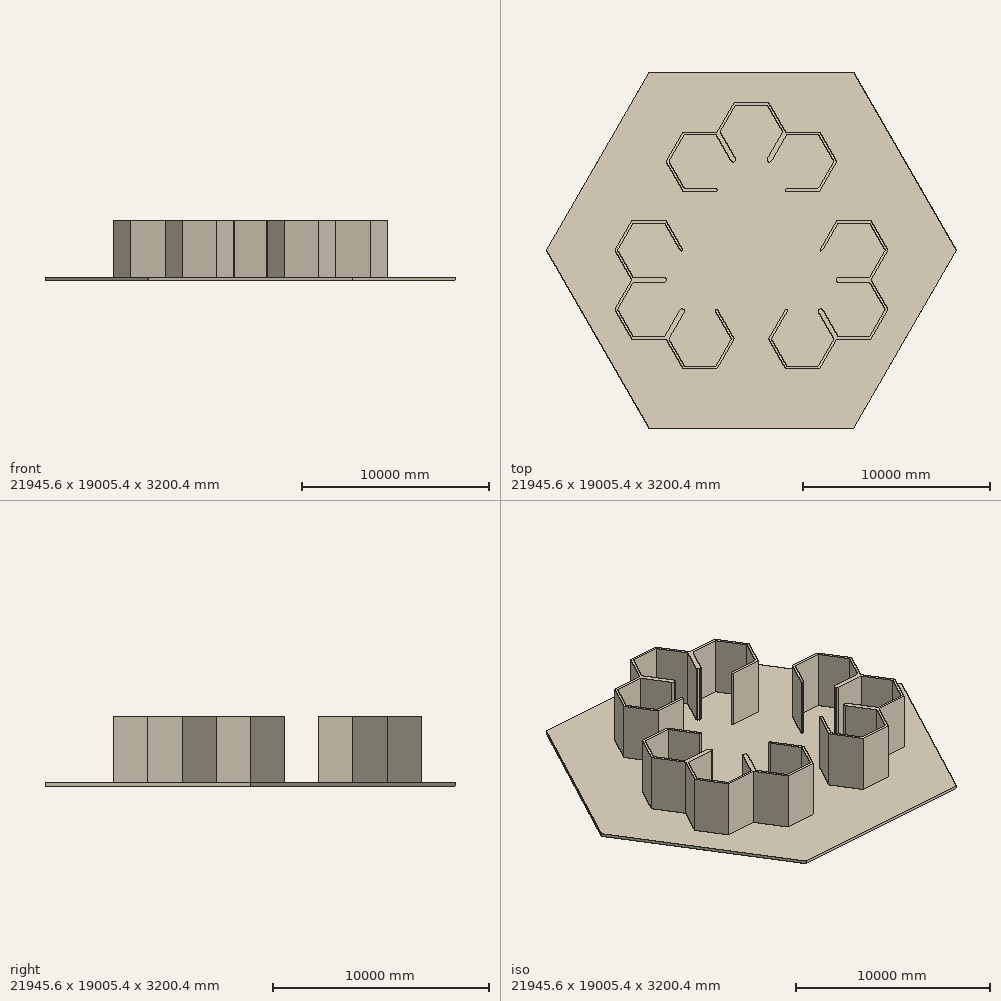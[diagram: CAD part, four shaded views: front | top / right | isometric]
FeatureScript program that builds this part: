
annotation { "Feature Type Name" : "Feature", "Feature Type Description" : "" }
export const myFeature = defineFeature(function(context is Context, id is Id, definition is map)
    precondition{}
    {
        {
            var Q0;
            Q0=qCreatedBy(makeId("Top.planeOp"),FACE);
            var sketch = newSketch(context, id + "F0", { "sketchPlane" : qUnion([Q0])});
            skLineSegment(sketch, "E0", {"start": v(0, 0) * mm, "end": v(1828.8, 0) * mm, "construction": true});
            skLineSegment(sketch, "E1", {"start": v(1828.8, 0) * mm, "end": v(3657.6, 0) * mm, "construction": true});
            skLineSegment(sketch, "E2", {"start": v(3657.6, 0) * mm, "end": v(5486.4, 0) * mm, "construction": true});
            skLineSegment(sketch, "E3", {"start": v(0, 0) * mm, "end": v(914.4, 1583.79) * mm, "construction": true});
            skLineSegment(sketch, "E4", {"start": v(914.4, 1583.79) * mm, "end": v(1828.8, 3167.57) * mm, "construction": true});
            skLineSegment(sketch, "E5", {"start": v(1828.8, 3167.57) * mm, "end": v(2743.2, 4751.36) * mm, "construction": true});
            skLineSegment(sketch, "E6", {"start": v(0, 0) * mm, "end": v(-914.4, 1583.79) * mm, "construction": true});
            skLineSegment(sketch, "E7", {"start": v(-914.4, 1583.79) * mm, "end": v(-1828.8, 3167.57) * mm, "construction": true});
            skLineSegment(sketch, "E8", {"start": v(-1828.8, 3167.57) * mm, "end": v(-2743.2, 4751.36) * mm, "construction": true});
            skLineSegment(sketch, "E9", {"start": v(0, 0) * mm, "end": v(-1828.8, 0) * mm, "construction": true});
            skLineSegment(sketch, "E10", {"start": v(-1828.8, 0) * mm, "end": v(-3657.6, 0) * mm, "construction": true});
            skLineSegment(sketch, "E11", {"start": v(-3657.6, 0) * mm, "end": v(-5486.4, 0) * mm, "construction": true});
            skLineSegment(sketch, "E12", {"start": v(0, 0) * mm, "end": v(-914.4, -1583.79) * mm, "construction": true});
            skLineSegment(sketch, "E13", {"start": v(-914.4, -1583.79) * mm, "end": v(-1828.8, -3167.57) * mm, "construction": true});
            skLineSegment(sketch, "E14", {"start": v(-1828.8, -3167.57) * mm, "end": v(-2743.2, -4751.36) * mm, "construction": true});
            skLineSegment(sketch, "E15", {"start": v(0, 0) * mm, "end": v(914.4, -1583.79) * mm, "construction": true});
            skLineSegment(sketch, "E16", {"start": v(914.4, -1583.79) * mm, "end": v(1828.8, -3167.57) * mm, "construction": true});
            skLineSegment(sketch, "E17", {"start": v(1828.8, -3167.57) * mm, "end": v(2743.2, -4751.36) * mm, "construction": true});
            skCircle(sketch, "E18.cCircle", {"center": v(0, 0) * mm, "radius": 1828.8 * mm, "construction": true});
            skLineSegment(sketch, "E18.0", {"start": v(1828.8, 0) * mm, "end": v(914.4, -1583.79) * mm});
            skLineSegment(sketch, "E18.1", {"start": v(914.4, -1583.79) * mm, "end": v(-914.4, -1583.79) * mm});
            skLineSegment(sketch, "E18.2", {"start": v(-914.4, -1583.79) * mm, "end": v(-1828.8, 0) * mm});
            skLineSegment(sketch, "E18.3", {"start": v(-1828.8, 0) * mm, "end": v(-914.4, 1583.79) * mm});
            skLineSegment(sketch, "E18.4", {"start": v(-914.4, 1583.79) * mm, "end": v(914.4, 1583.79) * mm});
            skLineSegment(sketch, "E18.5", {"start": v(914.4, 1583.79) * mm, "end": v(1828.8, 0) * mm});
            skLineSegment(sketch, "E19", {"start": v(914.4, -1583.79) * mm, "end": v(2743.2, -1583.79) * mm, "construction": true});
            skLineSegment(sketch, "E20", {"start": v(2743.2, -1583.79) * mm, "end": v(1828.8, 0) * mm, "construction": true});
            skCircle(sketch, "E21.cCircle", {"center": v(2743.2, -1583.79) * mm, "radius": 1828.8 * mm, "construction": true});
            skLineSegment(sketch, "E21.0", {"start": v(1828.8, 0) * mm, "end": v(3657.6, 0) * mm});
            skLineSegment(sketch, "E21.1", {"start": v(3657.6, 0) * mm, "end": v(4572, -1583.79) * mm});
            skLineSegment(sketch, "E21.2", {"start": v(4572, -1583.79) * mm, "end": v(3657.6, -3167.57) * mm});
            skLineSegment(sketch, "E21.3", {"start": v(3657.6, -3167.57) * mm, "end": v(1828.8, -3167.57) * mm});
            skLineSegment(sketch, "E21.4", {"start": v(1828.8, -3167.57) * mm, "end": v(914.4, -1583.79) * mm});
            skLineSegment(sketch, "E21.5", {"start": v(914.4, -1583.79) * mm, "end": v(1828.8, 0) * mm});
            skCircle(sketch, "E22.cCircle", {"center": v(5486.4, 0) * mm, "radius": 1828.8 * mm, "construction": true});
            skLineSegment(sketch, "E22.0", {"start": v(3657.6, 0) * mm, "end": v(4572, 1583.79) * mm});
            skLineSegment(sketch, "E22.1", {"start": v(4572, 1583.79) * mm, "end": v(6400.8, 1583.79) * mm});
            skLineSegment(sketch, "E22.2", {"start": v(6400.8, 1583.79) * mm, "end": v(7315.2, 0) * mm});
            skLineSegment(sketch, "E22.3", {"start": v(7315.2, 0) * mm, "end": v(6400.8, -1583.79) * mm});
            skLineSegment(sketch, "E22.4", {"start": v(6400.8, -1583.79) * mm, "end": v(4572, -1583.79) * mm});
            skLineSegment(sketch, "E22.5", {"start": v(4572, -1583.79) * mm, "end": v(3657.6, 0) * mm});
            skLineSegment(sketch, "E23", {"start": v(-914.4, -1583.79) * mm, "end": v(0, -3167.57) * mm, "construction": true});
            skLineSegment(sketch, "E24", {"start": v(914.4, -1583.79) * mm, "end": v(0, -3167.57) * mm, "construction": true});
            skCircle(sketch, "E25.cCircle", {"center": v(0, -3167.57) * mm, "radius": 1828.8 * mm, "construction": true});
            skLineSegment(sketch, "E25.0", {"start": v(914.4, -1583.79) * mm, "end": v(1828.8, -3167.57) * mm});
            skLineSegment(sketch, "E25.1", {"start": v(1828.8, -3167.57) * mm, "end": v(914.4, -4751.36) * mm});
            skLineSegment(sketch, "E25.2", {"start": v(914.4, -4751.36) * mm, "end": v(-914.4, -4751.36) * mm});
            skLineSegment(sketch, "E25.3", {"start": v(-914.4, -4751.36) * mm, "end": v(-1828.8, -3167.57) * mm});
            skLineSegment(sketch, "E25.4", {"start": v(-1828.8, -3167.57) * mm, "end": v(-914.4, -1583.79) * mm});
            skLineSegment(sketch, "E25.5", {"start": v(-914.4, -1583.79) * mm, "end": v(914.4, -1583.79) * mm});
            skLineSegment(sketch, "E26", {"start": v(1828.8, 0) * mm, "end": v(2743.2, 1583.79) * mm, "construction": true});
            skLineSegment(sketch, "E27", {"start": v(2743.2, 1583.79) * mm, "end": v(914.4, 1583.79) * mm, "construction": true});
            skLineSegment(sketch, "E28", {"start": v(914.4, 1583.79) * mm, "end": v(0, 3167.57) * mm, "construction": true});
            skLineSegment(sketch, "E29", {"start": v(0, 3167.57) * mm, "end": v(-914.4, 1583.79) * mm, "construction": true});
            skLineSegment(sketch, "E30", {"start": v(-914.4, 1583.79) * mm, "end": v(-2743.2, 1583.79) * mm, "construction": true});
            skLineSegment(sketch, "E31", {"start": v(-2743.2, 1583.79) * mm, "end": v(-1828.8, 0) * mm, "construction": true});
            skLineSegment(sketch, "E32", {"start": v(-1828.8, 0) * mm, "end": v(-2743.2, -1583.79) * mm, "construction": true});
            skLineSegment(sketch, "E33", {"start": v(-2743.2, -1583.79) * mm, "end": v(-914.4, -1583.79) * mm, "construction": true});
            skCircle(sketch, "E34.cCircle", {"center": v(2743.2, 1583.79) * mm, "radius": 1828.8 * mm, "construction": true});
            skLineSegment(sketch, "E34.0", {"start": v(914.4, 1583.79) * mm, "end": v(1828.8, 3167.57) * mm});
            skLineSegment(sketch, "E34.1", {"start": v(1828.8, 3167.57) * mm, "end": v(3657.6, 3167.57) * mm});
            skLineSegment(sketch, "E34.2", {"start": v(3657.6, 3167.57) * mm, "end": v(4572, 1583.79) * mm});
            skLineSegment(sketch, "E34.3", {"start": v(4572, 1583.79) * mm, "end": v(3657.6, 0) * mm});
            skLineSegment(sketch, "E34.4", {"start": v(3657.6, 0) * mm, "end": v(1828.8, 0) * mm});
            skLineSegment(sketch, "E34.5", {"start": v(1828.8, 0) * mm, "end": v(914.4, 1583.79) * mm});
            skCircle(sketch, "E35.cCircle", {"center": v(0, 3167.57) * mm, "radius": 1828.8 * mm, "construction": true});
            skLineSegment(sketch, "E35.0", {"start": v(-914.4, 1583.79) * mm, "end": v(-1828.8, 3167.57) * mm});
            skLineSegment(sketch, "E35.1", {"start": v(-1828.8, 3167.57) * mm, "end": v(-914.4, 4751.36) * mm});
            skLineSegment(sketch, "E35.2", {"start": v(-914.4, 4751.36) * mm, "end": v(914.4, 4751.36) * mm});
            skLineSegment(sketch, "E35.3", {"start": v(914.4, 4751.36) * mm, "end": v(1828.8, 3167.57) * mm});
            skLineSegment(sketch, "E35.4", {"start": v(1828.8, 3167.57) * mm, "end": v(914.4, 1583.79) * mm});
            skLineSegment(sketch, "E35.5", {"start": v(914.4, 1583.79) * mm, "end": v(-914.4, 1583.79) * mm});
            skCircle(sketch, "E36.cCircle", {"center": v(-2743.2, 1583.79) * mm, "radius": 1828.8 * mm, "construction": true});
            skLineSegment(sketch, "E36.0", {"start": v(-1828.8, 0) * mm, "end": v(-3657.6, 0) * mm});
            skLineSegment(sketch, "E36.1", {"start": v(-3657.6, 0) * mm, "end": v(-4572, 1583.79) * mm});
            skLineSegment(sketch, "E36.2", {"start": v(-4572, 1583.79) * mm, "end": v(-3657.6, 3167.57) * mm});
            skLineSegment(sketch, "E36.3", {"start": v(-3657.6, 3167.57) * mm, "end": v(-1828.8, 3167.57) * mm});
            skLineSegment(sketch, "E36.4", {"start": v(-1828.8, 3167.57) * mm, "end": v(-914.4, 1583.79) * mm});
            skLineSegment(sketch, "E36.5", {"start": v(-914.4, 1583.79) * mm, "end": v(-1828.8, 0) * mm});
            skCircle(sketch, "E37.cCircle", {"center": v(-2743.2, -1583.79) * mm, "radius": 1828.8 * mm, "construction": true});
            skLineSegment(sketch, "E37.0", {"start": v(-914.4, -1583.79) * mm, "end": v(-1828.8, -3167.57) * mm});
            skLineSegment(sketch, "E37.1", {"start": v(-1828.8, -3167.57) * mm, "end": v(-3657.6, -3167.57) * mm});
            skLineSegment(sketch, "E37.2", {"start": v(-3657.6, -3167.57) * mm, "end": v(-4572, -1583.79) * mm});
            skLineSegment(sketch, "E37.3", {"start": v(-4572, -1583.79) * mm, "end": v(-3657.6, 0) * mm});
            skLineSegment(sketch, "E37.4", {"start": v(-3657.6, 0) * mm, "end": v(-1828.8, 0) * mm});
            skLineSegment(sketch, "E37.5", {"start": v(-1828.8, 0) * mm, "end": v(-914.4, -1583.79) * mm});
            skCircle(sketch, "E38.cCircle", {"center": v(-2743.2, 4751.36) * mm, "radius": 1828.8 * mm, "construction": true});
            skLineSegment(sketch, "E38.0", {"start": v(-1828.8, 3167.57) * mm, "end": v(-3657.6, 3167.57) * mm});
            skLineSegment(sketch, "E38.1", {"start": v(-3657.6, 3167.57) * mm, "end": v(-4572, 4751.36) * mm});
            skLineSegment(sketch, "E38.2", {"start": v(-4572, 4751.36) * mm, "end": v(-3657.6, 6335.15) * mm});
            skLineSegment(sketch, "E38.3", {"start": v(-3657.6, 6335.15) * mm, "end": v(-1828.8, 6335.15) * mm});
            skLineSegment(sketch, "E38.4", {"start": v(-1828.8, 6335.15) * mm, "end": v(-914.4, 4751.36) * mm});
            skLineSegment(sketch, "E38.5", {"start": v(-914.4, 4751.36) * mm, "end": v(-1828.8, 3167.57) * mm});
            skCircle(sketch, "E39.cCircle", {"center": v(2743.2, 4751.36) * mm, "radius": 1828.8 * mm, "construction": true});
            skLineSegment(sketch, "E39.0", {"start": v(1828.8, 3167.57) * mm, "end": v(914.4, 4751.36) * mm});
            skLineSegment(sketch, "E39.1", {"start": v(914.4, 4751.36) * mm, "end": v(1828.8, 6335.15) * mm});
            skLineSegment(sketch, "E39.2", {"start": v(1828.8, 6335.15) * mm, "end": v(3657.6, 6335.15) * mm});
            skLineSegment(sketch, "E39.3", {"start": v(3657.6, 6335.15) * mm, "end": v(4572, 4751.36) * mm});
            skLineSegment(sketch, "E39.4", {"start": v(4572, 4751.36) * mm, "end": v(3657.6, 3167.57) * mm});
            skLineSegment(sketch, "E39.5", {"start": v(3657.6, 3167.57) * mm, "end": v(1828.8, 3167.57) * mm});
            skCircle(sketch, "E40.cCircle", {"center": v(-2743.2, -4751.36) * mm, "radius": 1828.8 * mm, "construction": true});
            skLineSegment(sketch, "E40.0", {"start": v(-1828.8, -3167.57) * mm, "end": v(-914.4, -4751.36) * mm});
            skLineSegment(sketch, "E40.1", {"start": v(-914.4, -4751.36) * mm, "end": v(-1828.8, -6335.15) * mm});
            skLineSegment(sketch, "E40.2", {"start": v(-1828.8, -6335.15) * mm, "end": v(-3657.6, -6335.15) * mm});
            skLineSegment(sketch, "E40.3", {"start": v(-3657.6, -6335.15) * mm, "end": v(-4572, -4751.36) * mm});
            skLineSegment(sketch, "E40.4", {"start": v(-4572, -4751.36) * mm, "end": v(-3657.6, -3167.57) * mm});
            skLineSegment(sketch, "E40.5", {"start": v(-3657.6, -3167.57) * mm, "end": v(-1828.8, -3167.57) * mm});
            skCircle(sketch, "E41.cCircle", {"center": v(-5486.4, 0) * mm, "radius": 1828.8 * mm, "construction": true});
            skLineSegment(sketch, "E41.0", {"start": v(-3657.6, 0) * mm, "end": v(-4572, -1583.79) * mm});
            skLineSegment(sketch, "E41.1", {"start": v(-4572, -1583.79) * mm, "end": v(-6400.8, -1583.79) * mm});
            skLineSegment(sketch, "E41.2", {"start": v(-6400.8, -1583.79) * mm, "end": v(-7315.2, 0) * mm});
            skLineSegment(sketch, "E41.3", {"start": v(-7315.2, 0) * mm, "end": v(-6400.8, 1583.79) * mm});
            skLineSegment(sketch, "E41.4", {"start": v(-6400.8, 1583.79) * mm, "end": v(-4572, 1583.79) * mm});
            skLineSegment(sketch, "E41.5", {"start": v(-4572, 1583.79) * mm, "end": v(-3657.6, 0) * mm});
            skLineSegment(sketch, "E42", {"start": v(-3657.6, -3167.57) * mm, "end": v(-5486.4, -3167.57) * mm, "construction": true});
            skLineSegment(sketch, "E43", {"start": v(-5486.4, -3167.57) * mm, "end": v(-4572, -1583.79) * mm, "construction": true});
            skCircle(sketch, "E44.cCircle", {"center": v(-5486.4, -3167.57) * mm, "radius": 1828.8 * mm, "construction": true});
            skLineSegment(sketch, "E44.0", {"start": v(-4572, -1583.79) * mm, "end": v(-3657.6, -3167.57) * mm});
            skLineSegment(sketch, "E44.1", {"start": v(-3657.6, -3167.57) * mm, "end": v(-4572, -4751.36) * mm});
            skLineSegment(sketch, "E44.2", {"start": v(-4572, -4751.36) * mm, "end": v(-6400.8, -4751.36) * mm});
            skLineSegment(sketch, "E44.3", {"start": v(-6400.8, -4751.36) * mm, "end": v(-7315.2, -3167.57) * mm});
            skLineSegment(sketch, "E44.4", {"start": v(-7315.2, -3167.57) * mm, "end": v(-6400.8, -1583.79) * mm});
            skLineSegment(sketch, "E44.5", {"start": v(-6400.8, -1583.79) * mm, "end": v(-4572, -1583.79) * mm});
            skLineSegment(sketch, "E45", {"start": v(-4572, 1583.79) * mm, "end": v(-5486.4, 3167.57) * mm, "construction": true});
            skPoint(sketch, "E45.endSnap0", {"position": v(-5486.4, 1583.79) * mm});
            skLineSegment(sketch, "E46", {"start": v(-5486.4, 3167.57) * mm, "end": v(-3657.6, 3167.57) * mm, "construction": true});
            skCircle(sketch, "E47.cCircle", {"center": v(-5486.4, 3167.57) * mm, "radius": 1828.8 * mm, "construction": true});
            skLineSegment(sketch, "E47.0", {"start": v(-3657.6, 3167.57) * mm, "end": v(-4572, 1583.79) * mm});
            skLineSegment(sketch, "E47.1", {"start": v(-4572, 1583.79) * mm, "end": v(-6400.8, 1583.79) * mm});
            skLineSegment(sketch, "E47.2", {"start": v(-6400.8, 1583.79) * mm, "end": v(-7315.2, 3167.57) * mm});
            skLineSegment(sketch, "E47.3", {"start": v(-7315.2, 3167.57) * mm, "end": v(-6400.8, 4751.36) * mm});
            skLineSegment(sketch, "E47.4", {"start": v(-6400.8, 4751.36) * mm, "end": v(-4572, 4751.36) * mm});
            skLineSegment(sketch, "E47.5", {"start": v(-4572, 4751.36) * mm, "end": v(-3657.6, 3167.57) * mm});
            skLineSegment(sketch, "E48", {"start": v(-914.4, 4751.36) * mm, "end": v(0, 6335.15) * mm, "construction": true});
            skLineSegment(sketch, "E49", {"start": v(0, 6335.15) * mm, "end": v(914.4, 4751.36) * mm, "construction": true});
            skLineSegment(sketch, "E50", {"start": v(3657.6, 3167.57) * mm, "end": v(5486.4, 3167.57) * mm, "construction": true});
            skLineSegment(sketch, "E51", {"start": v(5486.4, 3167.57) * mm, "end": v(4572, 1583.79) * mm, "construction": true});
            skLineSegment(sketch, "E52", {"start": v(4572, -1583.79) * mm, "end": v(5486.4, -3167.57) * mm, "construction": true});
            skLineSegment(sketch, "E53", {"start": v(5486.4, -3167.57) * mm, "end": v(3657.6, -3167.57) * mm, "construction": true});
            skLineSegment(sketch, "E54", {"start": v(-914.4, -4751.36) * mm, "end": v(0, -6335.15) * mm, "construction": true});
            skLineSegment(sketch, "E55", {"start": v(0, -6335.15) * mm, "end": v(914.4, -4751.36) * mm, "construction": true});
            skCircle(sketch, "E56.cCircle", {"center": v(2743.2, -4751.36) * mm, "radius": 1828.8 * mm, "construction": true});
            skLineSegment(sketch, "E56.0", {"start": v(1828.8, -3167.57) * mm, "end": v(3657.6, -3167.57) * mm});
            skLineSegment(sketch, "E56.1", {"start": v(3657.6, -3167.57) * mm, "end": v(4572, -4751.36) * mm});
            skLineSegment(sketch, "E56.2", {"start": v(4572, -4751.36) * mm, "end": v(3657.6, -6335.15) * mm});
            skLineSegment(sketch, "E56.3", {"start": v(3657.6, -6335.15) * mm, "end": v(1828.8, -6335.15) * mm});
            skLineSegment(sketch, "E56.4", {"start": v(1828.8, -6335.15) * mm, "end": v(914.4, -4751.36) * mm});
            skLineSegment(sketch, "E56.5", {"start": v(914.4, -4751.36) * mm, "end": v(1828.8, -3167.57) * mm});
            skCircle(sketch, "E57.cCircle", {"center": v(0, -6335.15) * mm, "radius": 1828.8 * mm, "construction": true});
            skLineSegment(sketch, "E57.0", {"start": v(914.4, -4751.36) * mm, "end": v(1828.8, -6335.15) * mm});
            skLineSegment(sketch, "E57.1", {"start": v(1828.8, -6335.15) * mm, "end": v(914.4, -7918.94) * mm});
            skLineSegment(sketch, "E57.2", {"start": v(914.4, -7918.94) * mm, "end": v(-914.4, -7918.94) * mm});
            skLineSegment(sketch, "E57.3", {"start": v(-914.4, -7918.94) * mm, "end": v(-1828.8, -6335.15) * mm});
            skLineSegment(sketch, "E57.4", {"start": v(-1828.8, -6335.15) * mm, "end": v(-914.4, -4751.36) * mm});
            skLineSegment(sketch, "E57.5", {"start": v(-914.4, -4751.36) * mm, "end": v(914.4, -4751.36) * mm});
            skCircle(sketch, "E58.cCircle", {"center": v(5486.4, -3167.57) * mm, "radius": 1828.8 * mm, "construction": true});
            skLineSegment(sketch, "E58.0", {"start": v(4572, -1583.79) * mm, "end": v(6400.8, -1583.79) * mm});
            skLineSegment(sketch, "E58.1", {"start": v(6400.8, -1583.79) * mm, "end": v(7315.2, -3167.57) * mm});
            skLineSegment(sketch, "E58.2", {"start": v(7315.2, -3167.57) * mm, "end": v(6400.8, -4751.36) * mm});
            skLineSegment(sketch, "E58.3", {"start": v(6400.8, -4751.36) * mm, "end": v(4572, -4751.36) * mm});
            skLineSegment(sketch, "E58.4", {"start": v(4572, -4751.36) * mm, "end": v(3657.6, -3167.57) * mm});
            skLineSegment(sketch, "E58.5", {"start": v(3657.6, -3167.57) * mm, "end": v(4572, -1583.79) * mm});
            skCircle(sketch, "E59.cCircle", {"center": v(5486.4, 3167.57) * mm, "radius": 1828.8 * mm, "construction": true});
            skLineSegment(sketch, "E59.0", {"start": v(3657.6, 3167.57) * mm, "end": v(4572, 4751.36) * mm});
            skLineSegment(sketch, "E59.1", {"start": v(4572, 4751.36) * mm, "end": v(6400.8, 4751.36) * mm});
            skLineSegment(sketch, "E59.2", {"start": v(6400.8, 4751.36) * mm, "end": v(7315.2, 3167.57) * mm});
            skLineSegment(sketch, "E59.3", {"start": v(7315.2, 3167.57) * mm, "end": v(6400.8, 1583.79) * mm});
            skLineSegment(sketch, "E59.4", {"start": v(6400.8, 1583.79) * mm, "end": v(4572, 1583.79) * mm});
            skLineSegment(sketch, "E59.5", {"start": v(4572, 1583.79) * mm, "end": v(3657.6, 3167.57) * mm});
            skCircle(sketch, "E60.cCircle", {"center": v(0, 6335.15) * mm, "radius": 1828.8 * mm, "construction": true});
            skLineSegment(sketch, "E60.0", {"start": v(-914.4, 4751.36) * mm, "end": v(-1828.8, 6335.15) * mm});
            skLineSegment(sketch, "E60.1", {"start": v(-1828.8, 6335.15) * mm, "end": v(-914.4, 7918.94) * mm});
            skLineSegment(sketch, "E60.2", {"start": v(-914.4, 7918.94) * mm, "end": v(914.4, 7918.94) * mm});
            skLineSegment(sketch, "E60.3", {"start": v(914.4, 7918.94) * mm, "end": v(1828.8, 6335.15) * mm});
            skLineSegment(sketch, "E60.4", {"start": v(1828.8, 6335.15) * mm, "end": v(914.4, 4751.36) * mm});
            skLineSegment(sketch, "E60.5", {"start": v(914.4, 4751.36) * mm, "end": v(-914.4, 4751.36) * mm});
            skLineSegment(sketch, "E61", {"start": v(-4572, 4751.36) * mm, "end": v(-5486.4, 6335.15) * mm, "construction": true});
            skPoint(sketch, "E61.endSnap0", {"position": v(-5486.4, 4751.36) * mm});
            skLineSegment(sketch, "E62", {"start": v(-5486.4, 6335.15) * mm, "end": v(-3657.6, 6335.15) * mm, "construction": true});
            skLineSegment(sketch, "E63", {"start": v(-1828.8, 6335.15) * mm, "end": v(-2743.2, 7918.94) * mm, "construction": true});
            skPoint(sketch, "E63.endSnap0", {"position": v(-2743.2, 6335.15) * mm});
            skLineSegment(sketch, "E64", {"start": v(-2743.2, 7918.94) * mm, "end": v(-3657.6, 6335.15) * mm, "construction": true});
            skLineSegment(sketch, "E65", {"start": v(-7315.2, 0) * mm, "end": v(-8229.6, 1583.79) * mm, "construction": true});
            skLineSegment(sketch, "E66", {"start": v(-8229.6, 1583.79) * mm, "end": v(-6400.8, 1583.79) * mm, "construction": true});
            skLineSegment(sketch, "E67", {"start": v(-8229.6, -1583.79) * mm, "end": v(-6400.8, -1583.79) * mm, "construction": true});
            skLineSegment(sketch, "E68", {"start": v(-7315.2, 0) * mm, "end": v(-8229.6, -1583.79) * mm, "construction": true});
            skLineSegment(sketch, "E69", {"start": v(-4572, -4751.36) * mm, "end": v(-5486.4, -6335.15) * mm, "construction": true});
            skPoint(sketch, "E69.endSnap0", {"position": v(-5486.4, -4751.36) * mm});
            skLineSegment(sketch, "E70", {"start": v(-5486.4, -6335.15) * mm, "end": v(-3657.6, -6335.15) * mm, "construction": true});
            skLineSegment(sketch, "E71", {"start": v(-1828.8, -6335.15) * mm, "end": v(-2743.2, -7918.94) * mm, "construction": true});
            skPoint(sketch, "E71.endSnap0", {"position": v(-2743.2, -6335.15) * mm});
            skLineSegment(sketch, "E72", {"start": v(-2743.2, -7918.94) * mm, "end": v(-3657.6, -6335.15) * mm, "construction": true});
            skLineSegment(sketch, "E73", {"start": v(1828.8, 6335.15) * mm, "end": v(2743.2, 7918.94) * mm, "construction": true});
            skLineSegment(sketch, "E74", {"start": v(2743.2, 7918.94) * mm, "end": v(3657.6, 6335.15) * mm, "construction": true});
            skLineSegment(sketch, "E75", {"start": v(3657.6, 6335.15) * mm, "end": v(5486.4, 6335.15) * mm, "construction": true});
            skPoint(sketch, "E75.endSnap0", {"position": v(5486.4, 4751.36) * mm});
            skLineSegment(sketch, "E76", {"start": v(5486.4, 6335.15) * mm, "end": v(4572, 4751.36) * mm, "construction": true});
            skLineSegment(sketch, "E77", {"start": v(7315.2, 0) * mm, "end": v(8229.6, 1583.79) * mm, "construction": true});
            skLineSegment(sketch, "E78", {"start": v(8229.6, 1583.79) * mm, "end": v(6400.8, 1583.79) * mm, "construction": true});
            skLineSegment(sketch, "E79", {"start": v(6400.8, -1583.79) * mm, "end": v(8229.6, -1583.79) * mm, "construction": true});
            skLineSegment(sketch, "E80", {"start": v(8229.6, -1583.79) * mm, "end": v(7315.2, 0) * mm, "construction": true});
            skLineSegment(sketch, "E81", {"start": v(1828.8, -6335.15) * mm, "end": v(2743.2, -7918.94) * mm, "construction": true});
            skPoint(sketch, "E81.endSnap0", {"position": v(2743.2, -6335.15) * mm});
            skLineSegment(sketch, "E82", {"start": v(2743.2, -7918.94) * mm, "end": v(3657.6, -6335.15) * mm, "construction": true});
            skLineSegment(sketch, "E83", {"start": v(4572, -4751.36) * mm, "end": v(5486.4, -6335.15) * mm, "construction": true});
            skPoint(sketch, "E83.endSnap0", {"position": v(5486.4, -4751.36) * mm});
            skLineSegment(sketch, "E84", {"start": v(5486.4, -6335.15) * mm, "end": v(3657.6, -6335.15) * mm, "construction": true});
            skCircle(sketch, "E85.cCircle", {"center": v(-2743.2, 7918.94) * mm, "radius": 1828.8 * mm, "construction": true});
            skLineSegment(sketch, "E85.0", {"start": v(-1828.8, 6335.15) * mm, "end": v(-3657.6, 6335.15) * mm});
            skLineSegment(sketch, "E85.1", {"start": v(-3657.6, 6335.15) * mm, "end": v(-4572, 7918.94) * mm});
            skLineSegment(sketch, "E85.2", {"start": v(-4572, 7918.94) * mm, "end": v(-3657.6, 9502.72) * mm});
            skLineSegment(sketch, "E85.3", {"start": v(-3657.6, 9502.72) * mm, "end": v(-1828.8, 9502.72) * mm});
            skLineSegment(sketch, "E85.4", {"start": v(-1828.8, 9502.72) * mm, "end": v(-914.4, 7918.94) * mm});
            skLineSegment(sketch, "E85.5", {"start": v(-914.4, 7918.94) * mm, "end": v(-1828.8, 6335.15) * mm});
            skCircle(sketch, "E86.cCircle", {"center": v(-5486.4, 6335.15) * mm, "radius": 1828.8 * mm, "construction": true});
            skLineSegment(sketch, "E86.0", {"start": v(-4572, 4751.36) * mm, "end": v(-6400.8, 4751.36) * mm});
            skLineSegment(sketch, "E86.1", {"start": v(-6400.8, 4751.36) * mm, "end": v(-7315.2, 6335.15) * mm});
            skLineSegment(sketch, "E86.2", {"start": v(-7315.2, 6335.15) * mm, "end": v(-6400.8, 7918.94) * mm});
            skLineSegment(sketch, "E86.3", {"start": v(-6400.8, 7918.94) * mm, "end": v(-4572, 7918.94) * mm});
            skLineSegment(sketch, "E86.4", {"start": v(-4572, 7918.94) * mm, "end": v(-3657.6, 6335.15) * mm});
            skLineSegment(sketch, "E86.5", {"start": v(-3657.6, 6335.15) * mm, "end": v(-4572, 4751.36) * mm});
            skCircle(sketch, "E87.cCircle", {"center": v(2743.2, 7918.94) * mm, "radius": 1828.8 * mm, "construction": true});
            skLineSegment(sketch, "E87.0", {"start": v(1828.8, 6335.15) * mm, "end": v(914.4, 7918.94) * mm});
            skLineSegment(sketch, "E87.1", {"start": v(914.4, 7918.94) * mm, "end": v(1828.8, 9502.72) * mm});
            skLineSegment(sketch, "E87.2", {"start": v(1828.8, 9502.72) * mm, "end": v(3657.6, 9502.72) * mm});
            skLineSegment(sketch, "E87.3", {"start": v(3657.6, 9502.72) * mm, "end": v(4572, 7918.94) * mm});
            skLineSegment(sketch, "E87.4", {"start": v(4572, 7918.94) * mm, "end": v(3657.6, 6335.15) * mm});
            skLineSegment(sketch, "E87.5", {"start": v(3657.6, 6335.15) * mm, "end": v(1828.8, 6335.15) * mm});
            skCircle(sketch, "E88.cCircle", {"center": v(5486.4, 6335.15) * mm, "radius": 1828.8 * mm, "construction": true});
            skLineSegment(sketch, "E88.0", {"start": v(4572, 4751.36) * mm, "end": v(3657.6, 6335.15) * mm});
            skLineSegment(sketch, "E88.1", {"start": v(3657.6, 6335.15) * mm, "end": v(4572, 7918.94) * mm});
            skLineSegment(sketch, "E88.2", {"start": v(4572, 7918.94) * mm, "end": v(6400.8, 7918.94) * mm});
            skLineSegment(sketch, "E88.3", {"start": v(6400.8, 7918.94) * mm, "end": v(7315.2, 6335.15) * mm});
            skLineSegment(sketch, "E88.4", {"start": v(7315.2, 6335.15) * mm, "end": v(6400.8, 4751.36) * mm});
            skLineSegment(sketch, "E88.5", {"start": v(6400.8, 4751.36) * mm, "end": v(4572, 4751.36) * mm});
            skCircle(sketch, "E89.cCircle", {"center": v(8229.6, -1583.79) * mm, "radius": 1828.8 * mm, "construction": true});
            skLineSegment(sketch, "E89.0", {"start": v(6400.8, -1583.79) * mm, "end": v(7315.2, 0) * mm});
            skLineSegment(sketch, "E89.1", {"start": v(7315.2, 0) * mm, "end": v(9144, 0) * mm});
            skLineSegment(sketch, "E89.2", {"start": v(9144, 0) * mm, "end": v(10058.4, -1583.79) * mm});
            skLineSegment(sketch, "E89.3", {"start": v(10058.4, -1583.79) * mm, "end": v(9144, -3167.57) * mm});
            skLineSegment(sketch, "E89.4", {"start": v(9144, -3167.57) * mm, "end": v(7315.2, -3167.57) * mm});
            skLineSegment(sketch, "E89.5", {"start": v(7315.2, -3167.57) * mm, "end": v(6400.8, -1583.79) * mm});
            skCircle(sketch, "E90.cCircle", {"center": v(8229.6, 1583.79) * mm, "radius": 1828.8 * mm, "construction": true});
            skLineSegment(sketch, "E90.0", {"start": v(6400.8, 1583.79) * mm, "end": v(7315.2, 3167.57) * mm});
            skLineSegment(sketch, "E90.1", {"start": v(7315.2, 3167.57) * mm, "end": v(9144, 3167.57) * mm});
            skLineSegment(sketch, "E90.2", {"start": v(9144, 3167.57) * mm, "end": v(10058.4, 1583.79) * mm});
            skLineSegment(sketch, "E90.3", {"start": v(10058.4, 1583.79) * mm, "end": v(9144, 0) * mm});
            skLineSegment(sketch, "E90.4", {"start": v(9144, 0) * mm, "end": v(7315.2, 0) * mm});
            skLineSegment(sketch, "E90.5", {"start": v(7315.2, 0) * mm, "end": v(6400.8, 1583.79) * mm});
            skCircle(sketch, "E91.cCircle", {"center": v(5486.4, -6335.15) * mm, "radius": 1828.8 * mm, "construction": true});
            skLineSegment(sketch, "E91.0", {"start": v(4572, -4751.36) * mm, "end": v(6400.8, -4751.36) * mm});
            skLineSegment(sketch, "E91.1", {"start": v(6400.8, -4751.36) * mm, "end": v(7315.2, -6335.15) * mm});
            skLineSegment(sketch, "E91.2", {"start": v(7315.2, -6335.15) * mm, "end": v(6400.8, -7918.94) * mm});
            skLineSegment(sketch, "E91.3", {"start": v(6400.8, -7918.94) * mm, "end": v(4572, -7918.94) * mm});
            skLineSegment(sketch, "E91.4", {"start": v(4572, -7918.94) * mm, "end": v(3657.6, -6335.15) * mm});
            skLineSegment(sketch, "E91.5", {"start": v(3657.6, -6335.15) * mm, "end": v(4572, -4751.36) * mm});
            skCircle(sketch, "E92.cCircle", {"center": v(2743.2, -7918.94) * mm, "radius": 1828.8 * mm, "construction": true});
            skLineSegment(sketch, "E92.0", {"start": v(1828.8, -6335.15) * mm, "end": v(3657.6, -6335.15) * mm});
            skLineSegment(sketch, "E92.1", {"start": v(3657.6, -6335.15) * mm, "end": v(4572, -7918.94) * mm});
            skLineSegment(sketch, "E92.2", {"start": v(4572, -7918.94) * mm, "end": v(3657.6, -9502.72) * mm});
            skLineSegment(sketch, "E92.3", {"start": v(3657.6, -9502.72) * mm, "end": v(1828.8, -9502.72) * mm});
            skLineSegment(sketch, "E92.4", {"start": v(1828.8, -9502.72) * mm, "end": v(914.4, -7918.94) * mm});
            skLineSegment(sketch, "E92.5", {"start": v(914.4, -7918.94) * mm, "end": v(1828.8, -6335.15) * mm});
            skCircle(sketch, "E93.cCircle", {"center": v(-2743.2, -7918.94) * mm, "radius": 1828.8 * mm, "construction": true});
            skLineSegment(sketch, "E93.0", {"start": v(-1828.8, -6335.15) * mm, "end": v(-914.4, -7918.94) * mm});
            skLineSegment(sketch, "E93.1", {"start": v(-914.4, -7918.94) * mm, "end": v(-1828.8, -9502.72) * mm});
            skLineSegment(sketch, "E93.2", {"start": v(-1828.8, -9502.72) * mm, "end": v(-3657.6, -9502.72) * mm});
            skLineSegment(sketch, "E93.3", {"start": v(-3657.6, -9502.72) * mm, "end": v(-4572, -7918.94) * mm});
            skLineSegment(sketch, "E93.4", {"start": v(-4572, -7918.94) * mm, "end": v(-3657.6, -6335.15) * mm});
            skLineSegment(sketch, "E93.5", {"start": v(-3657.6, -6335.15) * mm, "end": v(-1828.8, -6335.15) * mm});
            skCircle(sketch, "E94.cCircle", {"center": v(-5486.4, -6335.15) * mm, "radius": 1828.8 * mm, "construction": true});
            skLineSegment(sketch, "E94.0", {"start": v(-4572, -4751.36) * mm, "end": v(-3657.6, -6335.15) * mm});
            skLineSegment(sketch, "E94.1", {"start": v(-3657.6, -6335.15) * mm, "end": v(-4572, -7918.94) * mm});
            skLineSegment(sketch, "E94.2", {"start": v(-4572, -7918.94) * mm, "end": v(-6400.8, -7918.94) * mm});
            skLineSegment(sketch, "E94.3", {"start": v(-6400.8, -7918.94) * mm, "end": v(-7315.2, -6335.15) * mm});
            skLineSegment(sketch, "E94.4", {"start": v(-7315.2, -6335.15) * mm, "end": v(-6400.8, -4751.36) * mm});
            skLineSegment(sketch, "E94.5", {"start": v(-6400.8, -4751.36) * mm, "end": v(-4572, -4751.36) * mm});
            skCircle(sketch, "E95.cCircle", {"center": v(-8229.6, -1583.79) * mm, "radius": 1828.8 * mm, "construction": true});
            skLineSegment(sketch, "E95.0", {"start": v(-7315.2, 0) * mm, "end": v(-6400.8, -1583.79) * mm});
            skLineSegment(sketch, "E95.1", {"start": v(-6400.8, -1583.79) * mm, "end": v(-7315.2, -3167.57) * mm});
            skLineSegment(sketch, "E95.2", {"start": v(-7315.2, -3167.57) * mm, "end": v(-9144, -3167.57) * mm});
            skLineSegment(sketch, "E95.3", {"start": v(-9144, -3167.57) * mm, "end": v(-10058.4, -1583.79) * mm});
            skLineSegment(sketch, "E95.4", {"start": v(-10058.4, -1583.79) * mm, "end": v(-9144, 0) * mm});
            skLineSegment(sketch, "E95.5", {"start": v(-9144, 0) * mm, "end": v(-7315.2, 0) * mm});
            skCircle(sketch, "E96.cCircle", {"center": v(-8229.6, 1583.79) * mm, "radius": 1828.8 * mm, "construction": true});
            skLineSegment(sketch, "E96.0", {"start": v(-6400.8, 1583.79) * mm, "end": v(-7315.2, 0) * mm});
            skLineSegment(sketch, "E96.1", {"start": v(-7315.2, 0) * mm, "end": v(-9144, 0) * mm});
            skLineSegment(sketch, "E96.2", {"start": v(-9144, 0) * mm, "end": v(-10058.4, 1583.79) * mm});
            skLineSegment(sketch, "E96.3", {"start": v(-10058.4, 1583.79) * mm, "end": v(-9144, 3167.57) * mm});
            skLineSegment(sketch, "E96.4", {"start": v(-9144, 3167.57) * mm, "end": v(-7315.2, 3167.57) * mm});
            skLineSegment(sketch, "E96.5", {"start": v(-7315.2, 3167.57) * mm, "end": v(-6400.8, 1583.79) * mm});
            skLineSegment(sketch, "E97", {"start": v(-9144, 0) * mm, "end": v(-10972.8, 0) * mm, "construction": true});
            skCircle(sketch, "E98.cCircle", {"center": v(0, 0) * mm, "radius": 10972.8 * mm, "construction": true});
            skLineSegment(sketch, "E98.0", {"start": v(-10972.8, 0) * mm, "end": v(-5486.4, 9502.72) * mm});
            skLineSegment(sketch, "E98.1", {"start": v(-5486.4, 9502.72) * mm, "end": v(5486.4, 9502.72) * mm});
            skLineSegment(sketch, "E98.2", {"start": v(5486.4, 9502.72) * mm, "end": v(10972.8, 0) * mm});
            skLineSegment(sketch, "E98.3", {"start": v(10972.8, 0) * mm, "end": v(5486.4, -9502.72) * mm});
            skLineSegment(sketch, "E98.4", {"start": v(5486.4, -9502.72) * mm, "end": v(-5486.4, -9502.72) * mm});
            skLineSegment(sketch, "E98.5", {"start": v(-5486.4, -9502.72) * mm, "end": v(-10972.8, 0) * mm});
            skCircle(sketch, "E99.cCircle", {"center": v(-2743.2, 4751.36) * mm, "radius": 1676.4 * mm, "construction": true});
            skLineSegment(sketch, "E99.0", {"start": v(-1905, 3299.56) * mm, "end": v(-3581.4, 3299.56) * mm});
            skLineSegment(sketch, "E99.1", {"start": v(-3581.4, 3299.56) * mm, "end": v(-4419.6, 4751.36) * mm});
            skLineSegment(sketch, "E99.2", {"start": v(-4419.6, 4751.36) * mm, "end": v(-3581.4, 6203.17) * mm});
            skLineSegment(sketch, "E99.3", {"start": v(-3581.4, 6203.17) * mm, "end": v(-1905, 6203.17) * mm});
            skLineSegment(sketch, "E99.4", {"start": v(-1905, 6203.17) * mm, "end": v(-1066.8, 4751.36) * mm});
            skLineSegment(sketch, "E99.5", {"start": v(-1066.8, 4751.36) * mm, "end": v(-1905, 3299.56) * mm});
            skCircle(sketch, "E100.cCircle", {"center": v(0, 6335.15) * mm, "radius": 1676.4 * mm, "construction": true});
            skLineSegment(sketch, "E100.0", {"start": v(-838.2, 4883.34) * mm, "end": v(-1676.4, 6335.15) * mm});
            skLineSegment(sketch, "E100.1", {"start": v(-1676.4, 6335.15) * mm, "end": v(-838.2, 7786.95) * mm});
            skLineSegment(sketch, "E100.2", {"start": v(-838.2, 7786.95) * mm, "end": v(838.2, 7786.95) * mm});
            skLineSegment(sketch, "E100.3", {"start": v(838.2, 7786.95) * mm, "end": v(1676.4, 6335.15) * mm});
            skLineSegment(sketch, "E100.4", {"start": v(1676.4, 6335.15) * mm, "end": v(838.2, 4883.34) * mm});
            skLineSegment(sketch, "E100.5", {"start": v(838.2, 4883.34) * mm, "end": v(-838.2, 4883.34) * mm});
            skCircle(sketch, "E101.cCircle", {"center": v(2743.2, 4751.36) * mm, "radius": 1676.4 * mm, "construction": true});
            skLineSegment(sketch, "E101.0", {"start": v(1905, 3299.56) * mm, "end": v(1066.8, 4751.36) * mm});
            skLineSegment(sketch, "E101.1", {"start": v(1066.8, 4751.36) * mm, "end": v(1905, 6203.17) * mm});
            skLineSegment(sketch, "E101.2", {"start": v(1905, 6203.17) * mm, "end": v(3581.4, 6203.17) * mm});
            skLineSegment(sketch, "E101.3", {"start": v(3581.4, 6203.17) * mm, "end": v(4419.6, 4751.36) * mm});
            skLineSegment(sketch, "E101.4", {"start": v(4419.6, 4751.36) * mm, "end": v(3581.4, 3299.56) * mm});
            skLineSegment(sketch, "E101.5", {"start": v(3581.4, 3299.56) * mm, "end": v(1905, 3299.56) * mm});
            skCircle(sketch, "E102.cCircle", {"center": v(5486.4, 0) * mm, "radius": 1676.4 * mm, "construction": true});
            skLineSegment(sketch, "E102.0", {"start": v(3810, 0) * mm, "end": v(4648.2, 1451.8) * mm});
            skLineSegment(sketch, "E102.1", {"start": v(4648.2, 1451.8) * mm, "end": v(6324.6, 1451.8) * mm});
            skLineSegment(sketch, "E102.2", {"start": v(6324.6, 1451.8) * mm, "end": v(7162.8, 0) * mm});
            skLineSegment(sketch, "E102.3", {"start": v(7162.8, 0) * mm, "end": v(6324.6, -1451.8) * mm});
            skLineSegment(sketch, "E102.4", {"start": v(6324.6, -1451.8) * mm, "end": v(4648.2, -1451.8) * mm});
            skLineSegment(sketch, "E102.5", {"start": v(4648.2, -1451.8) * mm, "end": v(3810, 0) * mm});
            skCircle(sketch, "E103.cCircle", {"center": v(5486.4, -3167.57) * mm, "radius": 1676.4 * mm, "construction": true});
            skLineSegment(sketch, "E103.0", {"start": v(4648.2, -1715.77) * mm, "end": v(6324.6, -1715.77) * mm});
            skLineSegment(sketch, "E103.1", {"start": v(6324.6, -1715.77) * mm, "end": v(7162.8, -3167.57) * mm});
            skLineSegment(sketch, "E103.2", {"start": v(7162.8, -3167.57) * mm, "end": v(6324.6, -4619.38) * mm});
            skLineSegment(sketch, "E103.3", {"start": v(6324.6, -4619.38) * mm, "end": v(4648.2, -4619.38) * mm});
            skLineSegment(sketch, "E103.4", {"start": v(4648.2, -4619.38) * mm, "end": v(3810, -3167.57) * mm});
            skLineSegment(sketch, "E103.5", {"start": v(3810, -3167.57) * mm, "end": v(4648.2, -1715.77) * mm});
            skCircle(sketch, "E104.cCircle", {"center": v(2743.2, -4751.36) * mm, "radius": 1676.4 * mm, "construction": true});
            skLineSegment(sketch, "E104.0", {"start": v(1905, -3299.56) * mm, "end": v(3581.4, -3299.56) * mm});
            skLineSegment(sketch, "E104.1", {"start": v(3581.4, -3299.56) * mm, "end": v(4419.6, -4751.36) * mm});
            skLineSegment(sketch, "E104.2", {"start": v(4419.6, -4751.36) * mm, "end": v(3581.4, -6203.17) * mm});
            skLineSegment(sketch, "E104.3", {"start": v(3581.4, -6203.17) * mm, "end": v(1905, -6203.17) * mm});
            skLineSegment(sketch, "E104.4", {"start": v(1905, -6203.17) * mm, "end": v(1066.8, -4751.36) * mm});
            skLineSegment(sketch, "E104.5", {"start": v(1066.8, -4751.36) * mm, "end": v(1905, -3299.56) * mm});
            skCircle(sketch, "E105.cCircle", {"center": v(-2743.2, -4751.36) * mm, "radius": 1676.4 * mm, "construction": true});
            skLineSegment(sketch, "E105.0", {"start": v(-1905, -3299.56) * mm, "end": v(-1066.8, -4751.36) * mm});
            skLineSegment(sketch, "E105.1", {"start": v(-1066.8, -4751.36) * mm, "end": v(-1905, -6203.17) * mm});
            skLineSegment(sketch, "E105.2", {"start": v(-1905, -6203.17) * mm, "end": v(-3581.4, -6203.17) * mm});
            skLineSegment(sketch, "E105.3", {"start": v(-3581.4, -6203.17) * mm, "end": v(-4419.6, -4751.36) * mm});
            skLineSegment(sketch, "E105.4", {"start": v(-4419.6, -4751.36) * mm, "end": v(-3581.4, -3299.56) * mm});
            skLineSegment(sketch, "E105.5", {"start": v(-3581.4, -3299.56) * mm, "end": v(-1905, -3299.56) * mm});
            skCircle(sketch, "E106.cCircle", {"center": v(-5486.4, -3167.57) * mm, "radius": 1676.4 * mm, "construction": true});
            skLineSegment(sketch, "E106.0", {"start": v(-4648.2, -1715.77) * mm, "end": v(-3810, -3167.57) * mm});
            skLineSegment(sketch, "E106.1", {"start": v(-3810, -3167.57) * mm, "end": v(-4648.2, -4619.38) * mm});
            skLineSegment(sketch, "E106.2", {"start": v(-4648.2, -4619.38) * mm, "end": v(-6324.6, -4619.38) * mm});
            skLineSegment(sketch, "E106.3", {"start": v(-6324.6, -4619.38) * mm, "end": v(-7162.8, -3167.57) * mm});
            skLineSegment(sketch, "E106.4", {"start": v(-7162.8, -3167.57) * mm, "end": v(-6324.6, -1715.77) * mm});
            skLineSegment(sketch, "E106.5", {"start": v(-6324.6, -1715.77) * mm, "end": v(-4648.2, -1715.77) * mm});
            skCircle(sketch, "E107.cCircle", {"center": v(-5486.4, 0) * mm, "radius": 1676.4 * mm, "construction": true});
            skLineSegment(sketch, "E107.0", {"start": v(-3810, 0) * mm, "end": v(-4648.2, -1451.8) * mm});
            skLineSegment(sketch, "E107.1", {"start": v(-4648.2, -1451.8) * mm, "end": v(-6324.6, -1451.8) * mm});
            skLineSegment(sketch, "E107.2", {"start": v(-6324.6, -1451.8) * mm, "end": v(-7162.8, 0) * mm});
            skLineSegment(sketch, "E107.3", {"start": v(-7162.8, 0) * mm, "end": v(-6324.6, 1451.8) * mm});
            skLineSegment(sketch, "E107.4", {"start": v(-6324.6, 1451.8) * mm, "end": v(-4648.2, 1451.8) * mm});
            skLineSegment(sketch, "E107.5", {"start": v(-4648.2, 1451.8) * mm, "end": v(-3810, 0) * mm});
            skLineSegment(sketch, "E108", {"start": v(-1066.8, 4751.36) * mm, "end": v(-952.5, 4685.37) * mm});
            skLineSegment(sketch, "E109", {"start": v(-1905, 3299.56) * mm, "end": v(-1790.7, 3233.57) * mm});
            skLineSegment(sketch, "E110", {"start": v(-838.2, 4883.34) * mm, "end": v(-838.2, 4751.36) * mm});
            skLineSegment(sketch, "E111", {"start": v(838.2, 4883.34) * mm, "end": v(838.2, 4751.36) * mm});
            skLineSegment(sketch, "E112", {"start": v(1066.8, 4751.36) * mm, "end": v(952.5, 4685.37) * mm});
            skLineSegment(sketch, "E113", {"start": v(1905, 3299.56) * mm, "end": v(1790.7, 3233.57) * mm});
            skLineSegment(sketch, "E114", {"start": v(3810, 0) * mm, "end": v(3695.7, -66) * mm});
            skLineSegment(sketch, "E115", {"start": v(4648.2, -1451.8) * mm, "end": v(4533.9, -1517.8) * mm});
            skLineSegment(sketch, "E116", {"start": v(4648.2, -1715.77) * mm, "end": v(4533.9, -1649.78) * mm});
            skLineSegment(sketch, "E117", {"start": v(3810, -3167.57) * mm, "end": v(3695.7, -3101.58) * mm});
            skLineSegment(sketch, "E118", {"start": v(3581.4, -3299.56) * mm, "end": v(3581.4, -3167.57) * mm});
            skLineSegment(sketch, "E119", {"start": v(1905, -3299.56) * mm, "end": v(1905, -3167.57) * mm});
            skLineSegment(sketch, "E120", {"start": v(-3810, 0) * mm, "end": v(-3695.7, -66) * mm});
            skLineSegment(sketch, "E121", {"start": v(-4648.2, -1451.8) * mm, "end": v(-4533.9, -1517.8) * mm});
            skLineSegment(sketch, "E122", {"start": v(-4648.2, -1715.77) * mm, "end": v(-4533.9, -1649.78) * mm});
            skLineSegment(sketch, "E123", {"start": v(-3810, -3167.57) * mm, "end": v(-3695.7, -3101.58) * mm});
            skLineSegment(sketch, "E124", {"start": v(-3581.4, -3299.56) * mm, "end": v(-3581.4, -3167.57) * mm});
            skLineSegment(sketch, "E125", {"start": v(-1905, -3299.56) * mm, "end": v(-1905, -3167.57) * mm});
            skSolve(sketch);
        }
        {
            var Q0;
            {var subQ9=sQuery(id+"F0.wireOp",EDGE,"E95.4");var subQ10=makeQuery(id+"F0.imprint","IMPRINT",EDGE,{"derivedFrom":subQ9});var subQ12=sQuery(id+"F0.wireOp",EDGE,"E85.2");var subQ13=makeQuery(id+"F0.imprint","IMPRINT",EDGE,{"derivedFrom":subQ12});var subQ29=sQuery(id+"F0.wireOp",EDGE,"E87.3");var subQ30=makeQuery(id+"F0.imprint","IMPRINT",EDGE,{"derivedFrom":subQ29});var subQ31=sQuery(id+"F0.wireOp",EDGE,"E93.3");var subQ32=makeQuery(id+"F0.imprint","IMPRINT",EDGE,{"derivedFrom":subQ31});var subQ44=sQuery(id+"F0.wireOp",EDGE,"E91.3");var subQ45=makeQuery(id+"F0.imprint","IMPRINT",EDGE,{"derivedFrom":subQ44});var subQ60=sQuery(id+"F0.wireOp",EDGE,"E89.2");var subQ61=makeQuery(id+"F0.imprint","IMPRINT",EDGE,{"derivedFrom":subQ60});Q0=qUnion([makeQuery(id+"F0.imprint","IMPRINT",FACE,{"disambiguationData":[TD([[makeQuery(id+"F0.imprint","IMPRINT",EDGE,{"derivedFrom":sQuery(id+"F0.wireOp",EDGE,"E59.2")}),1.0]])]}),makeQuery(id+"F0.imprint","IMPRINT",FACE,{"disambiguationData":[TD([[subQ13,1.0]])]}),makeQuery(id+"F0.imprint","IMPRINT",FACE,{"disambiguationData":[TD([[makeQuery(id+"F0.imprint","IMPRINT",EDGE,{"derivedFrom":sQuery(id+"F0.wireOp",EDGE,"E58.2")}),1.0]])]}),makeQuery(id+"F0.imprint","IMPRINT",FACE,{"disambiguationData":[TD([[subQ30,1.0]])]}),makeQuery(id+"F0.imprint","IMPRINT",FACE,{"disambiguationData":[TD([[makeQuery(id+"F0.imprint","IMPRINT",EDGE,{"derivedFrom":sQuery(id+"F0.wireOp",EDGE,"E22.2")}),1.0]])]}),makeQuery(id+"F0.imprint","IMPRINT",FACE,{"disambiguationData":[TD([[makeQuery(id+"F0.imprint","IMPRINT",EDGE,{"derivedFrom":sQuery(id+"F0.wireOp",EDGE,"E40.3")}),1.0]])]}),makeQuery(id+"F0.imprint","IMPRINT",FACE,{"disambiguationData":[TD([[makeQuery(id+"F0.imprint","IMPRINT",EDGE,{"derivedFrom":sQuery(id+"F0.wireOp",EDGE,"E57.2")}),1.0]])]}),makeQuery(id+"F0.imprint","IMPRINT",FACE,{"disambiguationData":[TD([[subQ61,1.0]])]}),makeQuery(id+"F0.imprint","IMPRINT",FACE,{"disambiguationData":[TD([[makeQuery(id+"F0.imprint","IMPRINT",EDGE,{"derivedFrom":sQuery(id+"F0.wireOp",EDGE,"E60.2")}),1.0]])]}),makeQuery(id+"F0.imprint","IMPRINT",FACE,{"disambiguationData":[TD([[makeQuery(id+"F0.imprint","IMPRINT",EDGE,{"derivedFrom":sQuery(id+"F0.wireOp",EDGE,"E40.2")}),1.0]])]}),makeQuery(id+"F0.imprint","IMPRINT",FACE,{"disambiguationData":[TD([[makeQuery(id+"F0.imprint","IMPRINT",EDGE,{"derivedFrom":sQuery(id+"F0.wireOp",EDGE,"E22.3")}),1.0]])]}),makeQuery(id+"F0.imprint","IMPRINT",FACE,{"disambiguationData":[TD([[makeQuery(id+"F0.imprint","IMPRINT",EDGE,{"derivedFrom":sQuery(id+"F0.wireOp",EDGE,"E56.3")}),1.0]])]}),makeQuery(id+"F0.imprint","IMPRINT",FACE,{"disambiguationData":[TD([[makeQuery(id+"F0.imprint","IMPRINT",EDGE,{"derivedFrom":sQuery(id+"F0.wireOp",EDGE,"E47.3")}),1.0]])]}),makeQuery(id+"F0.imprint","IMPRINT",FACE,{"disambiguationData":[TD([[subQ45,1.0]])]}),makeQuery(id+"F0.imprint","IMPRINT",FACE,{"disambiguationData":[TD([[makeQuery(id+"F0.imprint","IMPRINT",EDGE,{"derivedFrom":sQuery(id+"F0.wireOp",EDGE,"E39.3")}),1.0]])]}),makeQuery(id+"F0.imprint","IMPRINT",FACE,{"disambiguationData":[TD([[makeQuery(id+"F0.imprint","IMPRINT",EDGE,{"derivedFrom":sQuery(id+"F0.wireOp",EDGE,"E56.2")}),1.0]])]}),makeQuery(id+"F0.imprint","IMPRINT",FACE,{"disambiguationData":[TD([[makeQuery(id+"F0.imprint","IMPRINT",EDGE,{"derivedFrom":sQuery(id+"F0.wireOp",EDGE,"E44.3")}),1.0]])]}),makeQuery(id+"F0.imprint","IMPRINT",FACE,{"disambiguationData":[TD([[subQ32,1.0]])]}),makeQuery(id+"F0.imprint","IMPRINT",FACE,{"disambiguationData":[TD([[makeQuery(id+"F0.imprint","IMPRINT",EDGE,{"derivedFrom":sQuery(id+"F0.wireOp",EDGE,"E39.2")}),1.0]])]}),makeQuery(id+"F0.imprint","IMPRINT",FACE,{"disambiguationData":[TD([[makeQuery(id+"F0.imprint","IMPRINT",EDGE,{"derivedFrom":sQuery(id+"F0.wireOp",EDGE,"E41.3")}),1.0]])]}),makeQuery(id+"F0.imprint","IMPRINT",FACE,{"disambiguationData":[TD([[subQ10,1.0]])]}),makeQuery(id+"F0.imprint","IMPRINT",FACE,{"disambiguationData":[TD([[makeQuery(id+"F0.imprint","IMPRINT",EDGE,{"derivedFrom":sQuery(id+"F0.wireOp",EDGE,"E38.3")}),1.0]])]}),makeQuery(id+"F0.imprint","IMPRINT",FACE,{"disambiguationData":[TD([[makeQuery(id+"F0.imprint","IMPRINT",EDGE,{"derivedFrom":sQuery(id+"F0.wireOp",EDGE,"E41.2")}),1.0]])]}),makeQuery(id+"F0.imprint","IMPRINT",FACE,{"disambiguationData":[TD([[makeQuery(id+"F0.imprint","IMPRINT",EDGE,{"derivedFrom":sQuery(id+"F0.wireOp",EDGE,"E38.2")}),1.0]])]})]);}
            var Q1;
            {var subQ0=sQuery(id+"F0.wireOp",EDGE,"E38.4");Q1=makeQuery(id+"F0.imprint","IMPRINT",FACE,{"disambiguationData":[TD([[makeQuery(id+"F0.imprint","IMPRINT",EDGE,{"derivedFrom":subQ0}),1.0]])]});}
            var Q2;
            {var subQ3=sQuery(id+"F0.wireOp",EDGE,"E36.3");Q2=makeQuery(id+"F0.imprint","IMPRINT",FACE,{"disambiguationData":[TD([[makeQuery(id+"F0.imprint","IMPRINT",EDGE,{"derivedFrom":subQ3}),1.0]])]});}
            var Q3;
            Q3=makeQuery(id+"F0.imprint","IMPRINT",FACE,{"disambiguationData":[TD([[makeQuery(id+"F0.imprint","IMPRINT",EDGE,{"derivedFrom":sQuery(id+"F0.wireOp",EDGE,"E36.2")}),1.0]])]});
            var Q4;
            {var subQ0=sQuery(id+"F0.wireOp",EDGE,"E36.1");Q4=makeQuery(id+"F0.imprint","IMPRINT",FACE,{"disambiguationData":[TD([[makeQuery(id+"F0.imprint","IMPRINT",EDGE,{"derivedFrom":subQ0}),1.0]])]});}
            var Q5;
            {var subQ3=sQuery(id+"F0.wireOp",EDGE,"E40.4");Q5=makeQuery(id+"F0.imprint","IMPRINT",FACE,{"disambiguationData":[TD([[makeQuery(id+"F0.imprint","IMPRINT",EDGE,{"derivedFrom":subQ3}),1.0]])]});}
            var Q6;
            {var subQ1=sQuery(id+"F0.wireOp",EDGE,"E25.3");Q6=makeQuery(id+"F0.imprint","IMPRINT",FACE,{"disambiguationData":[TD([[makeQuery(id+"F0.imprint","IMPRINT",EDGE,{"derivedFrom":subQ1}),1.0]])]});}
            var Q7;
            Q7=makeQuery(id+"F0.imprint","IMPRINT",FACE,{"disambiguationData":[TD([[makeQuery(id+"F0.imprint","IMPRINT",EDGE,{"derivedFrom":sQuery(id+"F0.wireOp",EDGE,"E25.2")}),1.0]])]});
            var Q8;
            {var subQ0=sQuery(id+"F0.wireOp",EDGE,"E25.1");Q8=makeQuery(id+"F0.imprint","IMPRINT",FACE,{"disambiguationData":[TD([[makeQuery(id+"F0.imprint","IMPRINT",EDGE,{"derivedFrom":subQ0}),1.0]])]});}
            var Q9;
            {var subQ4=sQuery(id+"F0.wireOp",EDGE,"E22.4");Q9=makeQuery(id+"F0.imprint","IMPRINT",FACE,{"disambiguationData":[TD([[makeQuery(id+"F0.imprint","IMPRINT",EDGE,{"derivedFrom":subQ4}),1.0]])]});}
            var Q10;
            {var subQ0=sQuery(id+"F0.wireOp",EDGE,"E22.0");Q10=makeQuery(id+"F0.imprint","IMPRINT",FACE,{"disambiguationData":[TD([[makeQuery(id+"F0.imprint","IMPRINT",EDGE,{"derivedFrom":subQ0}),-1.0]])]});}
            var Q11;
            Q11=makeQuery(id+"F0.imprint","IMPRINT",FACE,{"disambiguationData":[TD([[makeQuery(id+"F0.imprint","IMPRINT",EDGE,{"derivedFrom":sQuery(id+"F0.wireOp",EDGE,"E22.1")}),1.0]])]});
            var Q12;
            {var subQ0=sQuery(id+"F0.wireOp",EDGE,"E34.1");Q12=makeQuery(id+"F0.imprint","IMPRINT",FACE,{"disambiguationData":[TD([[makeQuery(id+"F0.imprint","IMPRINT",EDGE,{"derivedFrom":subQ0}),1.0]])]});}
            var Q13;
            Q13=makeQuery(id+"F0.imprint","IMPRINT",FACE,{"disambiguationData":[TD([[makeQuery(id+"F0.imprint","IMPRINT",EDGE,{"derivedFrom":sQuery(id+"F0.wireOp",EDGE,"E18.4")}),1.0]])]});
            var Q14;
            Q14=makeQuery(id+"F0.imprint","IMPRINT",FACE,{"disambiguationData":[TD([[makeQuery(id+"F0.imprint","IMPRINT",EDGE,{"derivedFrom":sQuery(id+"F0.wireOp",EDGE,"E18.3")}),1.0]])]});
            var Q15;
            Q15=makeQuery(id+"F0.imprint","IMPRINT",FACE,{"disambiguationData":[TD([[makeQuery(id+"F0.imprint","IMPRINT",EDGE,{"derivedFrom":sQuery(id+"F0.wireOp",EDGE,"E18.2")}),1.0]])]});
            var Q16;
            Q16=makeQuery(id+"F0.imprint","IMPRINT",FACE,{"disambiguationData":[TD([[makeQuery(id+"F0.imprint","IMPRINT",EDGE,{"derivedFrom":sQuery(id+"F0.wireOp",EDGE,"E18.1")}),1.0]])]});
            var Q17;
            Q17=makeQuery(id+"F0.imprint","IMPRINT",FACE,{"disambiguationData":[TD([[makeQuery(id+"F0.imprint","IMPRINT",EDGE,{"derivedFrom":sQuery(id+"F0.wireOp",EDGE,"E18.0")}),1.0]])]});
            var Q18;
            Q18=makeQuery(id+"F0.imprint","IMPRINT",FACE,{"disambiguationData":[TD([[makeQuery(id+"F0.imprint","IMPRINT",EDGE,{"derivedFrom":sQuery(id+"F0.wireOp",EDGE,"E18.5")}),1.0]])]});
            var Q19;
            Q19=makeQuery(id+"F0.imprint","IMPRINT",FACE,{"disambiguationData":[TD([[makeQuery(id+"F0.imprint","IMPRINT",EDGE,{"derivedFrom":sQuery(id+"F0.wireOp",EDGE,"E18.0")}),-1.0]])]});
            var Q20;
            Q20=makeQuery(id+"F0.imprint","IMPRINT",FACE,{"disambiguationData":[TD([[makeQuery(id+"F0.imprint","IMPRINT",EDGE,{"derivedFrom":sQuery(id+"F0.wireOp",EDGE,"E107.0")}),-1.0]])]});
            var Q21;
            Q21=makeQuery(id+"F0.imprint","IMPRINT",FACE,{"disambiguationData":[TD([[makeQuery(id+"F0.imprint","IMPRINT",EDGE,{"derivedFrom":sQuery(id+"F0.wireOp",EDGE,"E106.0")}),-1.0]])]});
            var Q22;
            Q22=makeQuery(id+"F0.imprint","IMPRINT",FACE,{"disambiguationData":[TD([[makeQuery(id+"F0.imprint","IMPRINT",EDGE,{"derivedFrom":sQuery(id+"F0.wireOp",EDGE,"E105.0")}),-1.0]])]});
            var Q23;
            Q23=makeQuery(id+"F0.imprint","IMPRINT",FACE,{"disambiguationData":[TD([[makeQuery(id+"F0.imprint","IMPRINT",EDGE,{"derivedFrom":sQuery(id+"F0.wireOp",EDGE,"E104.0")}),-1.0]])]});
            var Q24;
            Q24=makeQuery(id+"F0.imprint","IMPRINT",FACE,{"disambiguationData":[TD([[makeQuery(id+"F0.imprint","IMPRINT",EDGE,{"derivedFrom":sQuery(id+"F0.wireOp",EDGE,"E103.0")}),-1.0]])]});
            var Q25;
            Q25=makeQuery(id+"F0.imprint","IMPRINT",FACE,{"disambiguationData":[TD([[makeQuery(id+"F0.imprint","IMPRINT",EDGE,{"derivedFrom":sQuery(id+"F0.wireOp",EDGE,"E102.0")}),-1.0]])]});
            var Q26;
            Q26=makeQuery(id+"F0.imprint","IMPRINT",FACE,{"disambiguationData":[TD([[makeQuery(id+"F0.imprint","IMPRINT",EDGE,{"derivedFrom":sQuery(id+"F0.wireOp",EDGE,"E101.0")}),-1.0]])]});
            var Q27;
            Q27=makeQuery(id+"F0.imprint","IMPRINT",FACE,{"disambiguationData":[TD([[makeQuery(id+"F0.imprint","IMPRINT",EDGE,{"derivedFrom":sQuery(id+"F0.wireOp",EDGE,"E100.0")}),-1.0]])]});
            var Q28;
            Q28=makeQuery(id+"F0.imprint","IMPRINT",FACE,{"disambiguationData":[TD([[makeQuery(id+"F0.imprint","IMPRINT",EDGE,{"derivedFrom":sQuery(id+"F0.wireOp",EDGE,"E99.0")}),-1.0]])]});
            var Q29;
            Q29=makeQuery(id+"F0.imprint","IMPRINT",FACE,{"disambiguationData":[TD([[makeQuery(id+"F0.imprint","IMPRINT",EDGE,{"derivedFrom":sQuery(id+"F0.wireOp",EDGE,"E107.0")}),1.0]])]});
            var Q30;
            Q30=makeQuery(id+"F0.imprint","IMPRINT",FACE,{"disambiguationData":[TD([[makeQuery(id+"F0.imprint","IMPRINT",EDGE,{"derivedFrom":sQuery(id+"F0.wireOp",EDGE,"E106.0")}),1.0]])]});
            var Q31;
            Q31=makeQuery(id+"F0.imprint","IMPRINT",FACE,{"disambiguationData":[TD([[makeQuery(id+"F0.imprint","IMPRINT",EDGE,{"derivedFrom":sQuery(id+"F0.wireOp",EDGE,"E105.5")}),1.0]])]});
            var Q32;
            Q32=makeQuery(id+"F0.imprint","IMPRINT",FACE,{"disambiguationData":[TD([[makeQuery(id+"F0.imprint","IMPRINT",EDGE,{"derivedFrom":sQuery(id+"F0.wireOp",EDGE,"E101.0")}),1.0]])]});
            var Q33;
            Q33=makeQuery(id+"F0.imprint","IMPRINT",FACE,{"disambiguationData":[TD([[makeQuery(id+"F0.imprint","IMPRINT",EDGE,{"derivedFrom":sQuery(id+"F0.wireOp",EDGE,"E100.5")}),1.0]])]});
            var Q34;
            Q34=makeQuery(id+"F0.imprint","IMPRINT",FACE,{"disambiguationData":[TD([[makeQuery(id+"F0.imprint","IMPRINT",EDGE,{"derivedFrom":sQuery(id+"F0.wireOp",EDGE,"E99.5")}),1.0]])]});
            var Q35;
            Q35=makeQuery(id+"F0.imprint","IMPRINT",FACE,{"disambiguationData":[TD([[makeQuery(id+"F0.imprint","IMPRINT",EDGE,{"derivedFrom":sQuery(id+"F0.wireOp",EDGE,"E103.5")}),1.0]])]});
            var Q36;
            Q36=makeQuery(id+"F0.imprint","IMPRINT",FACE,{"disambiguationData":[TD([[makeQuery(id+"F0.imprint","IMPRINT",EDGE,{"derivedFrom":sQuery(id+"F0.wireOp",EDGE,"E104.0")}),1.0]])]});
            var Q37;
            Q37=makeQuery(id+"F0.imprint","IMPRINT",FACE,{"disambiguationData":[TD([[makeQuery(id+"F0.imprint","IMPRINT",EDGE,{"derivedFrom":sQuery(id+"F0.wireOp",EDGE,"E102.5")}),1.0]])]});
            extrude(context, id + "F1", {"entities" : qUnion([Q0, Q1, Q2, Q3, Q4, Q5, Q6, Q7, Q8, Q9, Q10, Q11, Q12, Q13, Q14, Q15, Q16, Q17, Q18, Q19, Q20, Q21, Q22, Q23, Q24, Q25, Q26, Q27, Q28, Q29, Q30, Q31, Q32, Q33, Q34, Q35, Q36, Q37]), "oppositeDirection" : true, "depth" : 152.4 * mm, "offsetDistance" : 30.48 * mm});
        }
        {
            var Q0;
            {var subQ0=sQuery(id+"F0.wireOp",EDGE,"E36.1");Q0=makeQuery(id+"F0.imprint","IMPRINT",FACE,{"disambiguationData":[TD([[makeQuery(id+"F0.imprint","IMPRINT",EDGE,{"derivedFrom":subQ0}),1.0]])]});}
            var Q1;
            {var subQ3=sQuery(id+"F0.wireOp",EDGE,"E40.4");Q1=makeQuery(id+"F0.imprint","IMPRINT",FACE,{"disambiguationData":[TD([[makeQuery(id+"F0.imprint","IMPRINT",EDGE,{"derivedFrom":subQ3}),1.0]])]});}
            var Q2;
            {var subQ1=sQuery(id+"F0.wireOp",EDGE,"E25.3");Q2=makeQuery(id+"F0.imprint","IMPRINT",FACE,{"disambiguationData":[TD([[makeQuery(id+"F0.imprint","IMPRINT",EDGE,{"derivedFrom":subQ1}),1.0]])]});}
            var Q3;
            {var subQ0=sQuery(id+"F0.wireOp",EDGE,"E25.1");Q3=makeQuery(id+"F0.imprint","IMPRINT",FACE,{"disambiguationData":[TD([[makeQuery(id+"F0.imprint","IMPRINT",EDGE,{"derivedFrom":subQ0}),1.0]])]});}
            var Q4;
            {var subQ4=sQuery(id+"F0.wireOp",EDGE,"E22.4");Q4=makeQuery(id+"F0.imprint","IMPRINT",FACE,{"disambiguationData":[TD([[makeQuery(id+"F0.imprint","IMPRINT",EDGE,{"derivedFrom":subQ4}),1.0]])]});}
            var Q5;
            {var subQ0=sQuery(id+"F0.wireOp",EDGE,"E22.0");Q5=makeQuery(id+"F0.imprint","IMPRINT",FACE,{"disambiguationData":[TD([[makeQuery(id+"F0.imprint","IMPRINT",EDGE,{"derivedFrom":subQ0}),-1.0]])]});}
            var Q6;
            {var subQ3=sQuery(id+"F0.wireOp",EDGE,"E36.3");Q6=makeQuery(id+"F0.imprint","IMPRINT",FACE,{"disambiguationData":[TD([[makeQuery(id+"F0.imprint","IMPRINT",EDGE,{"derivedFrom":subQ3}),1.0]])]});}
            var Q7;
            {var subQ0=sQuery(id+"F0.wireOp",EDGE,"E38.4");Q7=makeQuery(id+"F0.imprint","IMPRINT",FACE,{"disambiguationData":[TD([[makeQuery(id+"F0.imprint","IMPRINT",EDGE,{"derivedFrom":subQ0}),1.0]])]});}
            var Q8;
            {var subQ0=sQuery(id+"F0.wireOp",EDGE,"E34.1");Q8=makeQuery(id+"F0.imprint","IMPRINT",FACE,{"disambiguationData":[TD([[makeQuery(id+"F0.imprint","IMPRINT",EDGE,{"derivedFrom":subQ0}),1.0]])]});}
            extrude(context, id + "F2", {"entities" : qUnion([Q0, Q1, Q2, Q3, Q4, Q5, Q6, Q7, Q8]), "operationType" : NewBodyOperationType.ADD, "depth" : 3048 * mm, "offsetDistance" : 30.48 * mm});
        }
    });
